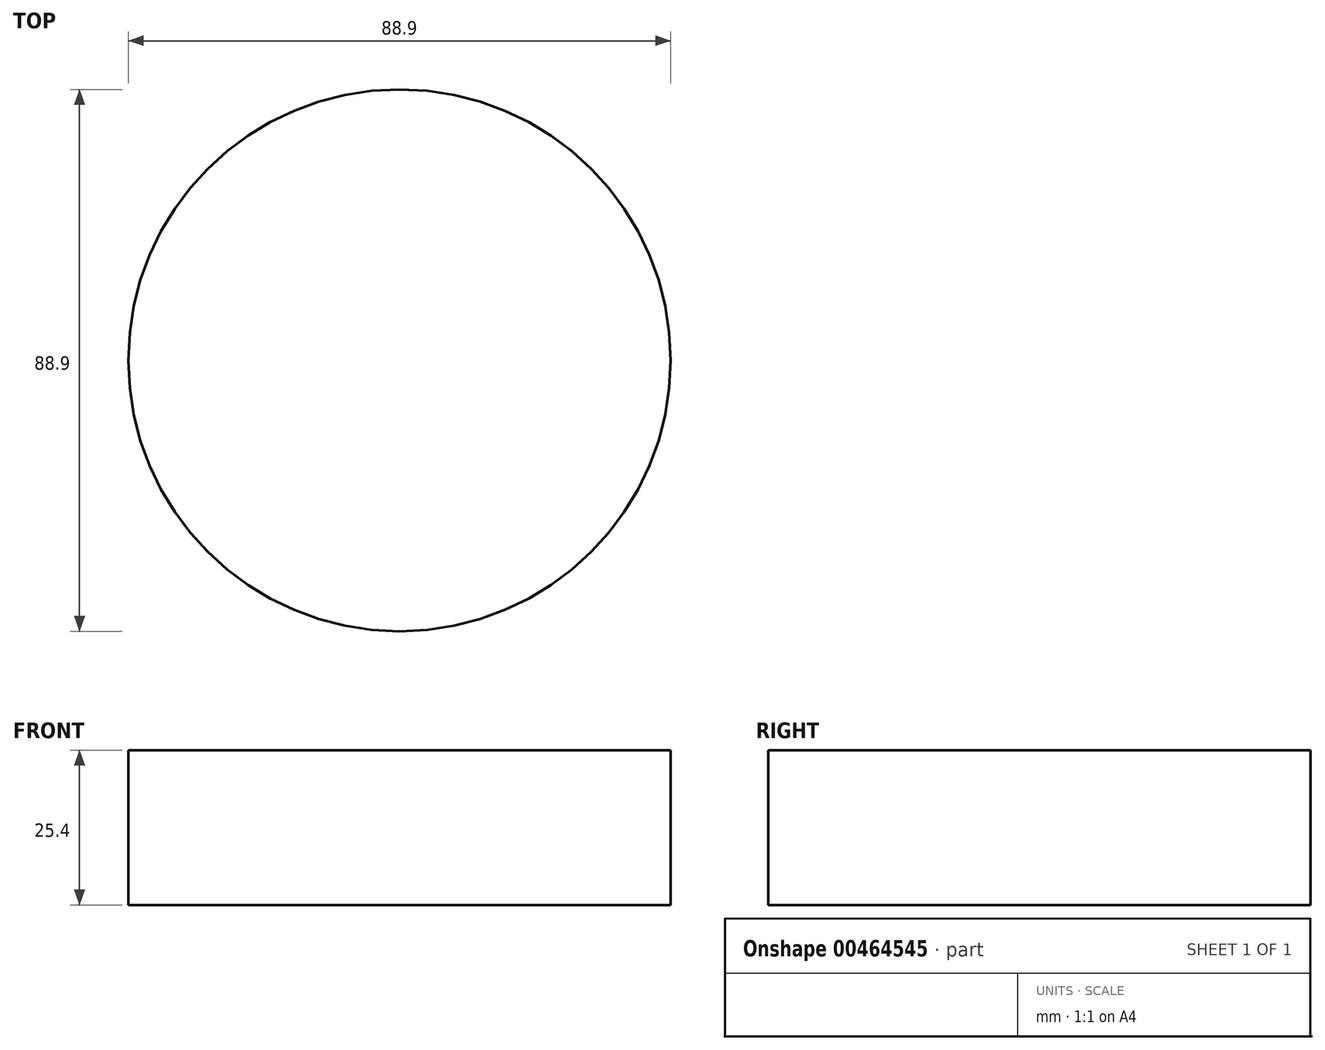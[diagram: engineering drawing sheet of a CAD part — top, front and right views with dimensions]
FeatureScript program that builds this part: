
annotation { "Feature Type Name" : "Feature", "Feature Type Description" : "" }
export const myFeature = defineFeature(function(context is Context, id is Id, definition is map)
    precondition{}
    {
        {
            var Q0;
            Q0=qCreatedBy(makeId("Top.planeOp"),FACE);
            var sketch = newSketch(context, id + "F0", { "sketchPlane" : qUnion([Q0])});
            skCircle(sketch, "E0", {"center": v(0, 0) * mm, "radius": 44.45 * mm});
            skSolve(sketch);
        }
        {
            var Q0;
            Q0 = qSketchRegion(id + "F0", true);
            extrude(context, id + "F1", {"entities" : qUnion([Q0]), "depth" : 25.4 * mm});
        }
    });
